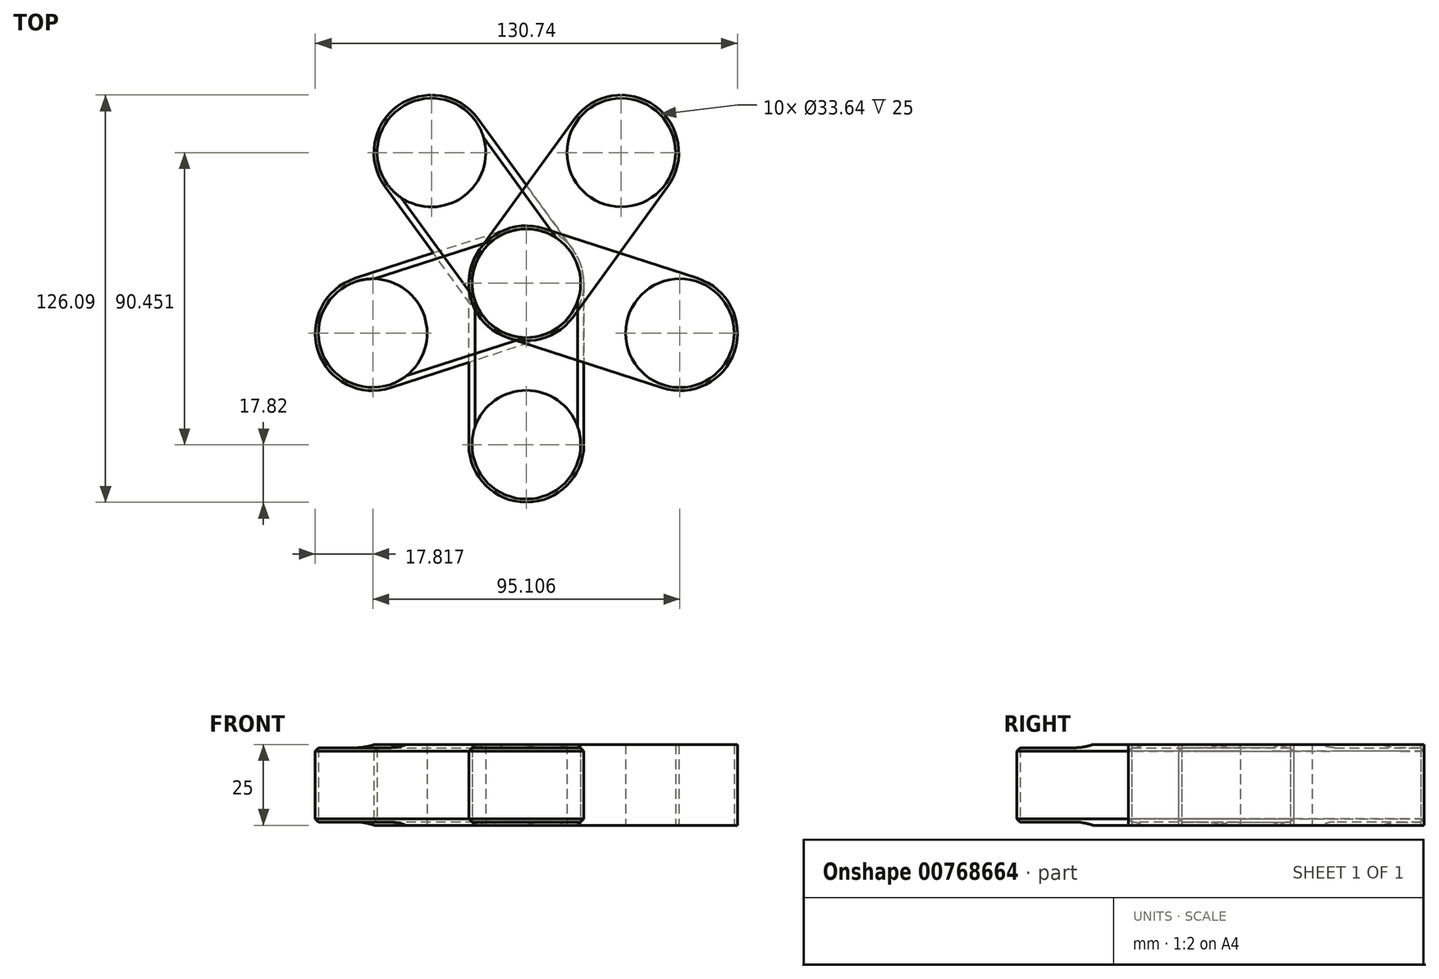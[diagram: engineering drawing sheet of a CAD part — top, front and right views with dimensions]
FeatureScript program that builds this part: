
annotation { "Feature Type Name" : "Feature", "Feature Type Description" : "" }
export const myFeature = defineFeature(function(context is Context, id is Id, definition is map)
    precondition{}
    {
        {
            var Q0;
            Q0=qCreatedBy(makeId("Top.planeOp"),FACE);
            var sketch = newSketch(context, id + "F0", { "sketchPlane" : qUnion([Q0])});
            skArc(sketch, "E0", {"start": v(0, 16.82) * mm, "mid": v(-16.82, 0) * mm, "end": v(0, -16.82) * mm});
            skArc(sketch, "E1.0", {"start": v(0, 17.82) * mm, "mid": v(-17.82, 0) * mm, "end": v(0, -17.82) * mm});
            skLineSegment(sketch, "E2.bottom", {"start": v(0, 0) * mm, "end": v(-17.82, 0) * mm});
            skLineSegment(sketch, "E2.top", {"start": v(0, -50) * mm, "end": v(-17.82, -50) * mm});
            skLineSegment(sketch, "E2.left", {"start": v(0, 0) * mm, "end": v(0, -50) * mm});
            skLineSegment(sketch, "E2.right", {"start": v(-17.82, 0) * mm, "end": v(-17.82, -50) * mm});
            skLineSegment(sketch, "E3", {"start": v(0, 0) * mm, "end": v(0, 31) * mm});
            skPoint(sketch, "E4.MirrorCS.end.orphan", {"position": v(-35.64, -16.82) * mm});
            skPoint(sketch, "E4.MirrorCS.start.orphan", {"position": v(-35.64, 16.82) * mm});
            skPoint(sketch, "E5.orphan", {"position": v(-35.64, 17.82) * mm});
            skPoint(sketch, "E6.MirrorCS.end.orphan", {"position": v(-35.64, -17.82) * mm});
            skArc(sketch, "E7", {"start": v(0, -32.18) * mm, "mid": v(-17.82, -50) * mm, "end": v(0, -67.82) * mm});
            skArc(sketch, "E8.0", {"start": v(0, -33.18) * mm, "mid": v(-16.82, -50) * mm, "end": v(0, -66.82) * mm});
            skLineSegment(sketch, "E9", {"start": v(0, -50) * mm, "end": v(0, -76.17) * mm});
            skSolve(sketch);
        }
        {
            var Q0;
            {var subQ0=sQuery(id+"F0.wireOp",EDGE,"E2.left");var subQ1=sQuery(id+"F0.wireOp",EDGE,"E1.0");var subQ2=makeQuery(id+"F0.imprint","INTERSECT",VERTEX,{"derivedFrom":[subQ1,subQ0]});Q0=makeQuery(id+"F0.imprint","IMPRINT",FACE,{"disambiguationData":[TD([[makeQuery(id+"F0.imprint","IMPRINT",EDGE,{"disambiguationData":[TD([[subQ2,1.0]])],"derivedFrom":subQ0}),-1.0]])]});}
            var Q1;
            {var subQ0=sQuery(id+"F0.wireOp",EDGE,"E3");var subQ1=sQuery(id+"F0.wireOp",EDGE,"E1.0");var subQ2=makeQuery(id+"F0.imprint","INTERSECT",VERTEX,{"derivedFrom":[subQ1,subQ0]});Q1=makeQuery(id+"F0.imprint","IMPRINT",FACE,{"disambiguationData":[TD([[makeQuery(id+"F0.imprint","IMPRINT",EDGE,{"disambiguationData":[TD([[subQ2,1.0]])],"derivedFrom":subQ0}),1.0]])]});}
            var Q2;
            {var subQ3=sQuery(id+"F0.wireOp",EDGE,"E2.right");Q2=makeQuery(id+"F0.imprint","IMPRINT",FACE,{"disambiguationData":[TD([[makeQuery(id+"F0.imprint","IMPRINT",EDGE,{"derivedFrom":subQ3}),1.0]])]});}
            var Q3;
            {var subQ3=sQuery(id+"F0.wireOp",EDGE,"E8.0");var subQ5=sQuery(id+"F0.wireOp",EDGE,"E9");var subQ7=makeQuery(id+"F0.imprint","INTERSECT",VERTEX,{"derivedFrom":[subQ3,subQ5]});Q3=makeQuery(id+"F0.imprint","IMPRINT",FACE,{"disambiguationData":[TD([[makeQuery(id+"F0.imprint","IMPRINT",EDGE,{"disambiguationData":[TD([[subQ7,1.0]])],"derivedFrom":subQ3}),-1.0]])]});}
            var Q4;
            {var subQ0=sQuery(id+"F0.wireOp",EDGE,"E7");var subQ5=sQuery(id+"F0.wireOp",EDGE,"E2.left");var subQ6=makeQuery(id+"F0.imprint","INTERSECT",VERTEX,{"derivedFrom":[subQ5,subQ0]});Q4=makeQuery(id+"F0.imprint","IMPRINT",FACE,{"disambiguationData":[TD([[makeQuery(id+"F0.imprint","IMPRINT",EDGE,{"disambiguationData":[TD([[subQ6,-1.0]])],"derivedFrom":subQ5}),-1.0]])]});}
            extrude(context, id + "F1", {"entities" : qUnion([Q0, Q1, Q2, Q3, Q4]), "depth" : 25 * mm, "offsetDistance" : 25 * mm});
        }
        {
            var Q0;
            Q0=makeQuery(id+"F1.opExtrude","SWEPT_BODY",BODY,{"disambiguationData":[OSD([sQuery(id+"F0.wireOp",EDGE,"E1.0"),sQuery(id+"F0.wireOp",EDGE,"E2.top"),sQuery(id+"F0.wireOp",EDGE,"E2.left"),sQuery(id+"F0.wireOp",EDGE,"E2.right"),sQuery(id+"F0.wireOp",EDGE,"E3"),sQuery(id+"F0.wireOp",EDGE,"E0")])]});
            var Q1;
            Q1=makeQuery(id+"F1.opExtrude","SWEPT_FACE",FACE,{"disambiguationData":[OSD([sQuery(id+"F0.wireOp",EDGE,"E2.left")])]});
            mirror(context, id + "F2", {"operationType" : NewBodyOperationType.ADD, "entities" : qUnion([Q0]), "mirrorPlane" : qUnion([Q1])});
        }
        {
            var Q0;
            Q0=makeQuery(id+"F1.opExtrude","SWEPT_BODY",BODY,{"disambiguationData":[OSD([sQuery(id+"F0.wireOp",EDGE,"E1.0"),sQuery(id+"F0.wireOp",EDGE,"E2.top"),sQuery(id+"F0.wireOp",EDGE,"E2.left"),sQuery(id+"F0.wireOp",EDGE,"E2.right"),sQuery(id+"F0.wireOp",EDGE,"E3"),sQuery(id+"F0.wireOp",EDGE,"E0")])]});
            var Q1;
            {var subQ0=makeQuery(id+"F1.opExtrude","SWEPT_FACE",FACE,{"disambiguationData":[OSD([sQuery(id+"F0.wireOp",EDGE,"E1.0")])]});Q1=makeQuery(id+"F2.boolean.opBoolean","MERGE",FACE,{"derivedFrom":[subQ0,makeQuery(id+"F2.opPattern","COPY",FACE,{"derivedFrom":subQ0,"instanceName":"1"})]});}
            circularPattern(context, id + "F3", {"entities" : qUnion([Q0]), "axis" : qUnion([Q1]), "angle" : 360 * degree, "instanceCount" : 5, "equalSpace" : true});
        }
        {
            var Q0;
            Q0=makeQuery(id+"F3.opPattern","COPY",EDGE,{"derivedFrom":makeQuery(id+"F1.opExtrude","CAP_EDGE",EDGE,{"disambiguationData":[OSD([sQuery(id+"F0.wireOp",EDGE,"E2.right")])],"isStart":true}),"instanceName":"1"});
            var Q1;
            Q1=makeQuery(id+"F3.opPattern","COPY",EDGE,{"derivedFrom":makeQuery(id+"F2.opPattern","COPY",EDGE,{"derivedFrom":makeQuery(id+"F1.opExtrude","CAP_EDGE",EDGE,{"disambiguationData":[OSD([sQuery(id+"F0.wireOp",EDGE,"E2.right")])],"isStart":true}),"instanceName":"1"}),"instanceName":"2"});
            var Q2;
            Q2=makeQuery(id+"F2.opPattern","COPY",EDGE,{"derivedFrom":makeQuery(id+"F1.opExtrude","CAP_EDGE",EDGE,{"disambiguationData":[OSD([sQuery(id+"F0.wireOp",EDGE,"E2.right")])],"isStart":true}),"instanceName":"1"});
            var Q3;
            Q3=makeQuery(id+"F2.opPattern","COPY",EDGE,{"derivedFrom":makeQuery(id+"F1.opExtrude","CAP_EDGE",EDGE,{"disambiguationData":[OSD([sQuery(id+"F0.wireOp",EDGE,"E2.right")])],"isStart":false}),"instanceName":"1"});
            var Q4;
            Q4=makeQuery(id+"F3.opPattern","COPY",EDGE,{"derivedFrom":makeQuery(id+"F1.opExtrude","CAP_EDGE",EDGE,{"disambiguationData":[OSD([sQuery(id+"F0.wireOp",EDGE,"E2.right")])],"isStart":false}),"instanceName":"2"});
            var Q5;
            Q5=makeQuery(id+"F3.opPattern","COPY",EDGE,{"derivedFrom":makeQuery(id+"F2.opPattern","COPY",EDGE,{"derivedFrom":makeQuery(id+"F1.opExtrude","CAP_EDGE",EDGE,{"disambiguationData":[OSD([sQuery(id+"F0.wireOp",EDGE,"E2.right")])],"isStart":false}),"instanceName":"1"}),"instanceName":"1"});
            chamfer(context, id + "F4", {"entities" : qUnion([Q0, Q1, Q2, Q3, Q4, Q5]), "width" : 2 * mm, "tangentPropagation" : true});
        }
    });
